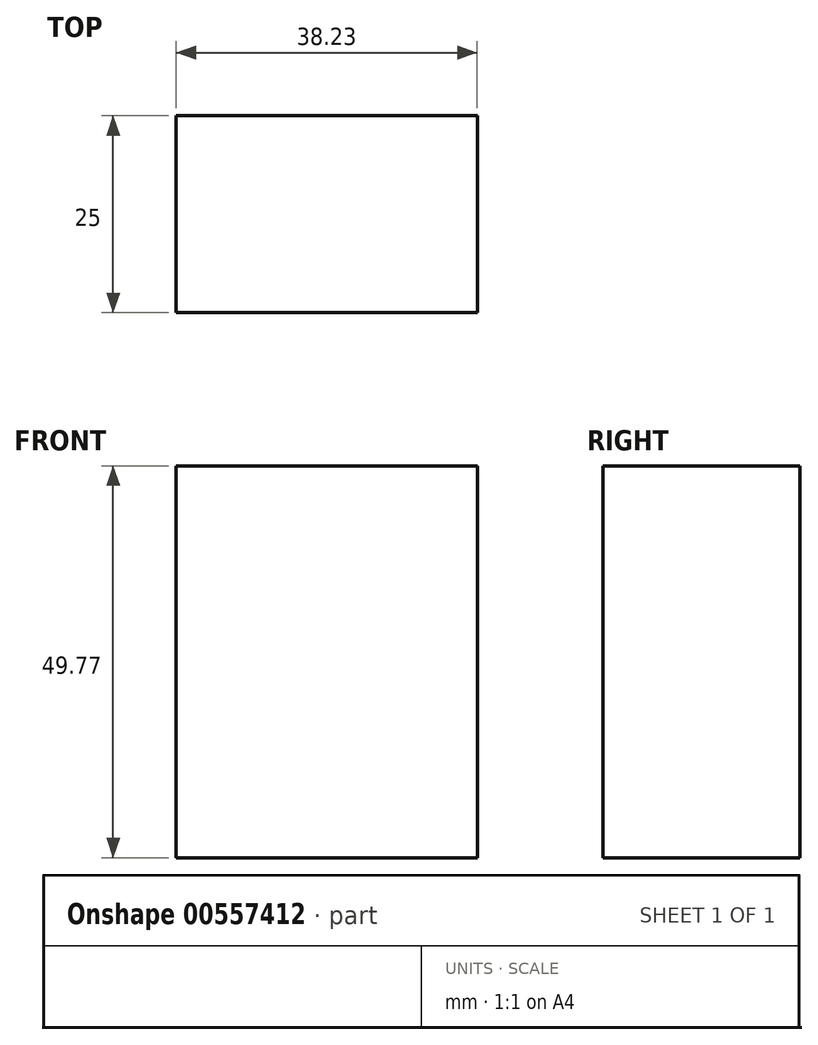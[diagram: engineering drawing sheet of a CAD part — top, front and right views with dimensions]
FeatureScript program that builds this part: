
annotation { "Feature Type Name" : "Feature", "Feature Type Description" : "" }
export const myFeature = defineFeature(function(context is Context, id is Id, definition is map)
    precondition{}
    {
        {
            var Q0;
            Q0=qCreatedBy(makeId("Front.planeOp"),FACE);
            var sketch = newSketch(context, id + "F0", { "sketchPlane" : qUnion([Q0])});
            skLineSegment(sketch, "E0.bottom", {"start": v(-16.84, 25.64) * mm, "end": v(21.4, 25.64) * mm});
            skLineSegment(sketch, "E0.top", {"start": v(-16.84, -24.13) * mm, "end": v(21.4, -24.13) * mm});
            skLineSegment(sketch, "E0.left", {"start": v(-16.84, 25.64) * mm, "end": v(-16.84, -24.13) * mm});
            skLineSegment(sketch, "E0.right", {"start": v(21.4, 25.64) * mm, "end": v(21.4, -24.13) * mm});
            skSolve(sketch);
        }
        {
            var Q0;
            Q0 = qSketchRegion(id + "F0", true);
            extrude(context, id + "F1", {"entities" : qUnion([Q0]), "depth" : 25 * mm, "offsetDistance" : 25 * mm});
        }
    });
